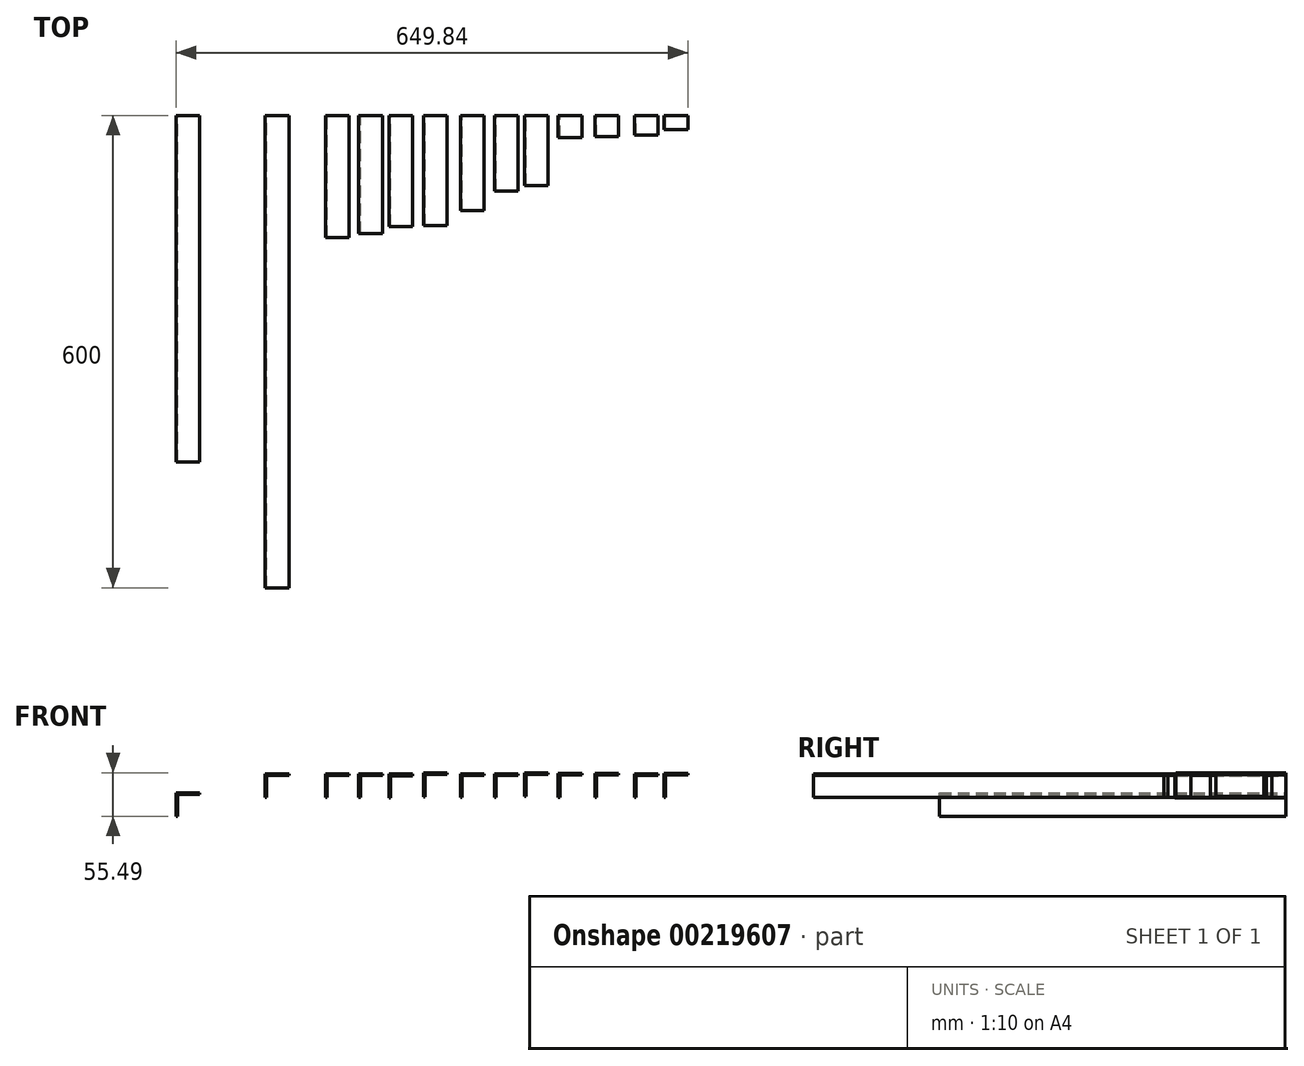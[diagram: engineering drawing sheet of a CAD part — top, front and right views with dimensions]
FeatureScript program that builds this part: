
annotation { "Feature Type Name" : "Feature", "Feature Type Description" : "" }
export const myFeature = defineFeature(function(context is Context, id is Id, definition is map)
    precondition{}
    {
        {
            var Q0;
            Q0=qCreatedBy(makeId("Front.planeOp"),FACE);
            var sketch = newSketch(context, id + "F0", { "sketchPlane" : qUnion([Q0])});
            skLineSegment(sketch, "E0", {"start": v(0, 0) * mm, "end": v(0, 30) * mm});
            skLineSegment(sketch, "E1", {"start": v(0, 30) * mm, "end": v(30, 30) * mm});
            skLineSegment(sketch, "E2.0", {"start": v(2, 0) * mm, "end": v(2, 28) * mm});
            skLineSegment(sketch, "E3.0", {"start": v(2, 28) * mm, "end": v(30, 28) * mm});
            skLineSegment(sketch, "E4", {"start": v(30, 30) * mm, "end": v(30, 28) * mm});
            skLineSegment(sketch, "E5", {"start": v(0, 0) * mm, "end": v(2, 0) * mm});
            skPoint(sketch, "E6.endSnap0", {"position": v(16, 28) * mm});
            skPoint(sketch, "E7.startSnap0", {"position": v(0, 15) * mm});
            skLineSegment(sketch, "E8", {"start": v(42.13, 0.37) * mm, "end": v(42.13, 30.37) * mm});
            skLineSegment(sketch, "E9", {"start": v(42.13, 30.37) * mm, "end": v(72.13, 30.37) * mm});
            skLineSegment(sketch, "E10.0", {"start": v(44.13, 0.37) * mm, "end": v(44.13, 28.37) * mm});
            skLineSegment(sketch, "E11.0", {"start": v(44.13, 28.37) * mm, "end": v(72.13, 28.37) * mm});
            skLineSegment(sketch, "E12", {"start": v(72.13, 30.37) * mm, "end": v(72.13, 28.37) * mm});
            skLineSegment(sketch, "E13", {"start": v(42.13, 0.37) * mm, "end": v(44.13, 0.37) * mm});
            skLineSegment(sketch, "E14", {"start": v(80.62, -0.15) * mm, "end": v(80.62, 29.85) * mm});
            skLineSegment(sketch, "E15", {"start": v(80.62, 29.85) * mm, "end": v(110.62, 29.85) * mm});
            skLineSegment(sketch, "E16.0", {"start": v(82.62, -0.15) * mm, "end": v(82.62, 27.85) * mm});
            skLineSegment(sketch, "E17.0", {"start": v(82.62, 27.85) * mm, "end": v(110.62, 27.85) * mm});
            skLineSegment(sketch, "E18", {"start": v(110.62, 29.85) * mm, "end": v(110.62, 27.85) * mm});
            skLineSegment(sketch, "E19", {"start": v(80.62, -0.15) * mm, "end": v(82.62, -0.15) * mm});
            skLineSegment(sketch, "E20", {"start": v(124.5, 1.16) * mm, "end": v(124.5, 31.16) * mm});
            skLineSegment(sketch, "E21", {"start": v(124.5, 31.16) * mm, "end": v(154.5, 31.16) * mm});
            skLineSegment(sketch, "E22.0", {"start": v(126.5, 1.16) * mm, "end": v(126.5, 29.16) * mm});
            skLineSegment(sketch, "E23.0", {"start": v(126.5, 29.16) * mm, "end": v(154.5, 29.16) * mm});
            skLineSegment(sketch, "E24", {"start": v(154.5, 31.16) * mm, "end": v(154.5, 29.16) * mm});
            skLineSegment(sketch, "E25", {"start": v(124.5, 1.16) * mm, "end": v(126.5, 1.16) * mm});
            skLineSegment(sketch, "E26", {"start": v(171.47, 0.28) * mm, "end": v(171.47, 30.28) * mm});
            skLineSegment(sketch, "E27", {"start": v(171.47, 30.28) * mm, "end": v(201.47, 30.28) * mm});
            skLineSegment(sketch, "E28.0", {"start": v(173.47, 0.28) * mm, "end": v(173.47, 28.28) * mm});
            skLineSegment(sketch, "E29.0", {"start": v(173.47, 28.28) * mm, "end": v(201.47, 28.28) * mm});
            skLineSegment(sketch, "E30", {"start": v(201.47, 30.28) * mm, "end": v(201.47, 28.28) * mm});
            skLineSegment(sketch, "E31", {"start": v(171.47, 0.28) * mm, "end": v(173.47, 0.28) * mm});
            skLineSegment(sketch, "E32", {"start": v(214.49, 0.28) * mm, "end": v(214.49, 30.28) * mm});
            skLineSegment(sketch, "E33", {"start": v(214.49, 30.28) * mm, "end": v(244.49, 30.28) * mm});
            skLineSegment(sketch, "E34.0", {"start": v(216.49, 0.28) * mm, "end": v(216.49, 28.28) * mm});
            skLineSegment(sketch, "E35.0", {"start": v(216.49, 28.28) * mm, "end": v(244.49, 28.28) * mm});
            skLineSegment(sketch, "E36", {"start": v(244.49, 30.28) * mm, "end": v(244.49, 28.28) * mm});
            skLineSegment(sketch, "E37", {"start": v(214.49, 0.28) * mm, "end": v(216.49, 0.28) * mm});
            skLineSegment(sketch, "E38", {"start": v(252.68, 1.54) * mm, "end": v(252.68, 31.54) * mm});
            skLineSegment(sketch, "E39", {"start": v(252.68, 31.54) * mm, "end": v(282.68, 31.54) * mm});
            skLineSegment(sketch, "E40.0", {"start": v(254.68, 1.54) * mm, "end": v(254.68, 29.54) * mm});
            skLineSegment(sketch, "E41.0", {"start": v(254.68, 29.54) * mm, "end": v(282.68, 29.54) * mm});
            skLineSegment(sketch, "E42", {"start": v(282.68, 31.54) * mm, "end": v(282.68, 29.54) * mm});
            skLineSegment(sketch, "E43", {"start": v(252.68, 1.54) * mm, "end": v(254.68, 1.54) * mm});
            skLineSegment(sketch, "E44", {"start": v(295.54, 0.55) * mm, "end": v(295.54, 30.55) * mm});
            skLineSegment(sketch, "E45", {"start": v(295.54, 30.55) * mm, "end": v(325.54, 30.55) * mm});
            skLineSegment(sketch, "E46.0", {"start": v(297.54, 0.55) * mm, "end": v(297.54, 28.55) * mm});
            skLineSegment(sketch, "E47.0", {"start": v(297.54, 28.55) * mm, "end": v(325.54, 28.55) * mm});
            skLineSegment(sketch, "E48", {"start": v(325.54, 30.55) * mm, "end": v(325.54, 28.55) * mm});
            skLineSegment(sketch, "E49", {"start": v(295.54, 0.55) * mm, "end": v(297.54, 0.55) * mm});
            skLineSegment(sketch, "E50", {"start": v(342.34, 0.55) * mm, "end": v(342.34, 30.55) * mm});
            skLineSegment(sketch, "E51", {"start": v(342.34, 30.55) * mm, "end": v(372.34, 30.55) * mm});
            skLineSegment(sketch, "E52.0", {"start": v(344.34, 0.55) * mm, "end": v(344.34, 28.55) * mm});
            skLineSegment(sketch, "E53.0", {"start": v(344.34, 28.55) * mm, "end": v(372.34, 28.55) * mm});
            skLineSegment(sketch, "E54", {"start": v(372.34, 30.55) * mm, "end": v(372.34, 28.55) * mm});
            skLineSegment(sketch, "E55", {"start": v(342.34, 0.55) * mm, "end": v(344.34, 0.55) * mm});
            skLineSegment(sketch, "E56", {"start": v(392.1, 0.06) * mm, "end": v(392.1, 30.06) * mm});
            skLineSegment(sketch, "E57", {"start": v(392.1, 30.06) * mm, "end": v(422.1, 30.06) * mm});
            skLineSegment(sketch, "E58.0", {"start": v(394.1, 0.06) * mm, "end": v(394.1, 28.06) * mm});
            skLineSegment(sketch, "E59.0", {"start": v(394.1, 28.06) * mm, "end": v(422.1, 28.06) * mm});
            skLineSegment(sketch, "E60", {"start": v(422.1, 30.06) * mm, "end": v(422.1, 28.06) * mm});
            skLineSegment(sketch, "E61", {"start": v(392.1, 0.06) * mm, "end": v(394.1, 0.06) * mm});
            skLineSegment(sketch, "E62", {"start": v(430.04, 0.55) * mm, "end": v(430.04, 30.55) * mm});
            skLineSegment(sketch, "E63", {"start": v(430.04, 30.55) * mm, "end": v(460.04, 30.55) * mm});
            skLineSegment(sketch, "E64.0", {"start": v(432.04, 0.55) * mm, "end": v(432.04, 28.55) * mm});
            skLineSegment(sketch, "E65.0", {"start": v(432.04, 28.55) * mm, "end": v(460.04, 28.55) * mm});
            skLineSegment(sketch, "E66", {"start": v(460.04, 30.55) * mm, "end": v(460.04, 28.55) * mm});
            skLineSegment(sketch, "E67", {"start": v(430.04, 0.55) * mm, "end": v(432.04, 0.55) * mm});
            skLineSegment(sketch, "E68", {"start": v(-76.67, 0.18) * mm, "end": v(-76.67, 30.18) * mm});
            skLineSegment(sketch, "E69", {"start": v(-76.67, 30.18) * mm, "end": v(-46.67, 30.18) * mm});
            skLineSegment(sketch, "E70.0", {"start": v(-74.67, 0.18) * mm, "end": v(-74.67, 28.18) * mm});
            skLineSegment(sketch, "E71.0", {"start": v(-74.67, 28.18) * mm, "end": v(-46.67, 28.18) * mm});
            skLineSegment(sketch, "E72", {"start": v(-46.67, 30.18) * mm, "end": v(-46.67, 28.18) * mm});
            skLineSegment(sketch, "E73", {"start": v(-76.67, 0.18) * mm, "end": v(-74.67, 0.18) * mm});
            skLineSegment(sketch, "E74", {"start": v(-189.8, -23.95) * mm, "end": v(-189.8, 6.05) * mm});
            skLineSegment(sketch, "E75", {"start": v(-189.8, 6.05) * mm, "end": v(-159.8, 6.05) * mm});
            skLineSegment(sketch, "E76.0", {"start": v(-187.8, -23.95) * mm, "end": v(-187.8, 4.05) * mm});
            skLineSegment(sketch, "E77.0", {"start": v(-187.8, 4.05) * mm, "end": v(-159.8, 4.05) * mm});
            skLineSegment(sketch, "E78", {"start": v(-159.8, 6.05) * mm, "end": v(-159.8, 4.05) * mm});
            skLineSegment(sketch, "E79", {"start": v(-189.8, -23.95) * mm, "end": v(-187.8, -23.95) * mm});
            skSolve(sketch);
        }
        {
            var Q0;
            Q0=makeQuery(id+"F0.imprint","IMPRINT",FACE,{"disambiguationData":[TD([[makeQuery(id+"F0.imprint","IMPRINT",EDGE,{"derivedFrom":sQuery(id+"F0.wireOp",EDGE,"E0")}),-1.0]])]});
            extrude(context, id + "F1", {"entities" : qUnion([Q0]), "depth" : 155 * mm});
        }
        {
            var Q0;
            Q0=makeQuery(id+"F0.imprint","IMPRINT",FACE,{"disambiguationData":[TD([[makeQuery(id+"F0.imprint","IMPRINT",EDGE,{"derivedFrom":sQuery(id+"F0.wireOp",EDGE,"E8")}),-1.0]])]});
            extrude(context, id + "F2", {"entities" : qUnion([Q0]), "depth" : 150 * mm});
        }
        {
            var Q0;
            Q0=makeQuery(id+"F0.imprint","IMPRINT",FACE,{"disambiguationData":[TD([[makeQuery(id+"F0.imprint","IMPRINT",EDGE,{"derivedFrom":sQuery(id+"F0.wireOp",EDGE,"E14")}),-1.0]])]});
            extrude(context, id + "F3", {"entities" : qUnion([Q0]), "depth" : 141 * mm});
        }
        {
            var Q0;
            Q0=makeQuery(id+"F0.imprint","IMPRINT",FACE,{"disambiguationData":[TD([[makeQuery(id+"F0.imprint","IMPRINT",EDGE,{"derivedFrom":sQuery(id+"F0.wireOp",EDGE,"E20")}),-1.0]])]});
            extrude(context, id + "F4", {"entities" : qUnion([Q0]), "depth" : 140 * mm});
        }
        {
            var Q0;
            Q0=makeQuery(id+"F0.imprint","IMPRINT",FACE,{"disambiguationData":[TD([[makeQuery(id+"F0.imprint","IMPRINT",EDGE,{"derivedFrom":sQuery(id+"F0.wireOp",EDGE,"E26")}),-1.0]])]});
            extrude(context, id + "F5", {"entities" : qUnion([Q0]), "depth" : 121 * mm});
        }
        {
            var Q0;
            Q0=makeQuery(id+"F0.imprint","IMPRINT",FACE,{"disambiguationData":[TD([[makeQuery(id+"F0.imprint","IMPRINT",EDGE,{"derivedFrom":sQuery(id+"F0.wireOp",EDGE,"E32")}),-1.0]])]});
            extrude(context, id + "F6", {"entities" : qUnion([Q0]), "depth" : 96 * mm});
        }
        {
            var Q0;
            Q0=makeQuery(id+"F0.imprint","IMPRINT",FACE,{"disambiguationData":[TD([[makeQuery(id+"F0.imprint","IMPRINT",EDGE,{"derivedFrom":sQuery(id+"F0.wireOp",EDGE,"E38")}),-1.0]])]});
            extrude(context, id + "F7", {"entities" : qUnion([Q0]), "depth" : 89 * mm});
        }
        {
            var Q0;
            Q0=makeQuery(id+"F0.imprint","IMPRINT",FACE,{"disambiguationData":[TD([[makeQuery(id+"F0.imprint","IMPRINT",EDGE,{"derivedFrom":sQuery(id+"F0.wireOp",EDGE,"E44")}),-1.0]])]});
            extrude(context, id + "F8", {"entities" : qUnion([Q0]), "depth" : 28 * mm});
        }
        {
            var Q0;
            Q0=makeQuery(id+"F0.imprint","IMPRINT",FACE,{"disambiguationData":[TD([[makeQuery(id+"F0.imprint","IMPRINT",EDGE,{"derivedFrom":sQuery(id+"F0.wireOp",EDGE,"E50")}),-1.0]])]});
            extrude(context, id + "F9", {"entities" : qUnion([Q0]), "depth" : 27 * mm});
        }
        {
            var Q0;
            Q0=makeQuery(id+"F0.imprint","IMPRINT",FACE,{"disambiguationData":[TD([[makeQuery(id+"F0.imprint","IMPRINT",EDGE,{"derivedFrom":sQuery(id+"F0.wireOp",EDGE,"E56")}),-1.0]])]});
            extrude(context, id + "F10", {"entities" : qUnion([Q0]), "depth" : 25 * mm});
        }
        {
            var Q0;
            Q0=makeQuery(id+"F0.imprint","IMPRINT",FACE,{"disambiguationData":[TD([[makeQuery(id+"F0.imprint","IMPRINT",EDGE,{"derivedFrom":sQuery(id+"F0.wireOp",EDGE,"E62")}),-1.0]])]});
            extrude(context, id + "F11", {"entities" : qUnion([Q0]), "depth" : 18 * mm});
        }
        {
            var Q0;
            Q0=makeQuery(id+"F0.imprint","IMPRINT",FACE,{"disambiguationData":[TD([[makeQuery(id+"F0.imprint","IMPRINT",EDGE,{"derivedFrom":sQuery(id+"F0.wireOp",EDGE,"E68")}),-1.0]])]});
            extrude(context, id + "F12", {"entities" : qUnion([Q0]), "depth" : 600 * mm});
        }
        {
            var Q0;
            Q0=makeQuery(id+"F0.imprint","IMPRINT",FACE,{"disambiguationData":[TD([[makeQuery(id+"F0.imprint","IMPRINT",EDGE,{"derivedFrom":sQuery(id+"F0.wireOp",EDGE,"E74")}),-1.0]])]});
            var Q1;
            Q1=sQuery(id+"F0.wireOp",EDGE,"E74");
            var Q2;
            Q2=sQuery(id+"F0.wireOp",EDGE,"E75");
            var Q3;
            Q3=sQuery(id+"F0.wireOp",EDGE,"E76.0");
            var Q4;
            Q4=sQuery(id+"F0.wireOp",EDGE,"E77.0");
            var Q5;
            Q5=sQuery(id+"F0.wireOp",EDGE,"E78");
            var Q6;
            Q6=sQuery(id+"F0.wireOp",EDGE,"E79");
            extrude(context, id + "F13", {"entities" : qUnion([Q0]), "surfaceEntities" : qUnion([Q1, Q2, Q3, Q4, Q5, Q6]), "depth" : 440 * mm});
        }
    });
